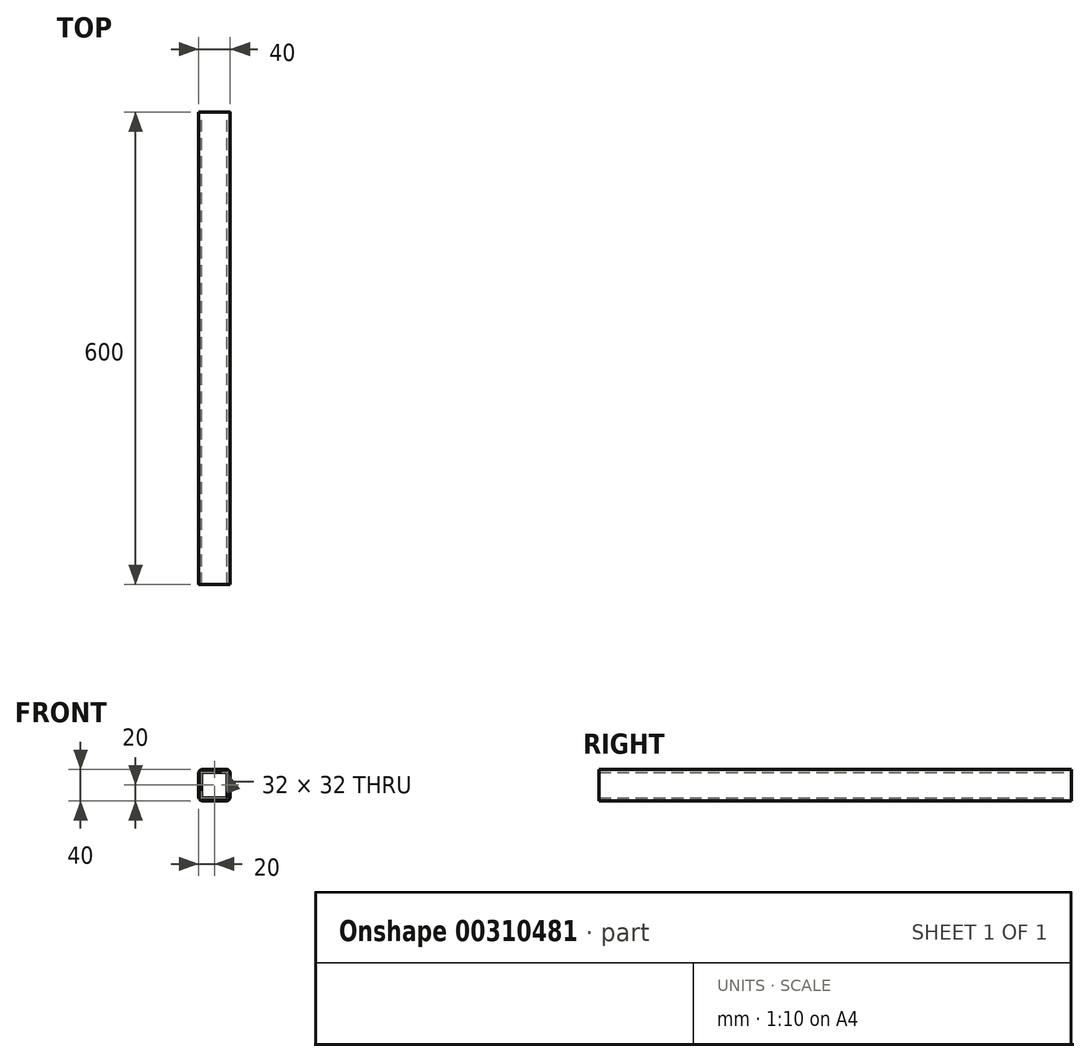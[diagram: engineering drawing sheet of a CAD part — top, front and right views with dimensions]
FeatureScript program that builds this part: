
annotation { "Feature Type Name" : "Feature", "Feature Type Description" : "" }
export const myFeature = defineFeature(function(context is Context, id is Id, definition is map)
    precondition{}
    {
        {
            var Q0;
            Q0=qCreatedBy(makeId("Front.planeOp"),FACE);
            var sketch = newSketch(context, id + "F0", { "sketchPlane" : qUnion([Q0])});
            skLineSegment(sketch, "E0.bottom", {"start": v(15, -20) * mm, "end": v(-15, -20) * mm});
            skLineSegment(sketch, "E0.top", {"start": v(15, 20) * mm, "end": v(-15, 20) * mm});
            skLineSegment(sketch, "E0.left", {"start": v(20, -15) * mm, "end": v(20, 15) * mm});
            skLineSegment(sketch, "E0.right", {"start": v(-20, -15) * mm, "end": v(-20, 15) * mm});
            skPoint(sketch, "E0.middle", {"position": v(0, 0) * mm});
            skPoint(sketch, "E1.visualSharp", {"position": v(-20, 20) * mm});
            skArc(sketch, "E1.filletArc", {"start": v(-15, 20) * mm, "mid": v(-18.54, 18.54) * mm, "end": v(-20, 15) * mm});
            skPoint(sketch, "E2.visualSharp", {"position": v(20, 20) * mm});
            skArc(sketch, "E2.filletArc", {"start": v(20, 15) * mm, "mid": v(18.54, 18.54) * mm, "end": v(15, 20) * mm});
            skPoint(sketch, "E3.visualSharp", {"position": v(20, -20) * mm});
            skArc(sketch, "E3.filletArc", {"start": v(15, -20) * mm, "mid": v(18.54, -18.54) * mm, "end": v(20, -15) * mm});
            skPoint(sketch, "E4.visualSharp", {"position": v(-20, -20) * mm});
            skArc(sketch, "E4.filletArc", {"start": v(-20, -15) * mm, "mid": v(-18.54, -18.54) * mm, "end": v(-15, -20) * mm});
            skLineSegment(sketch, "E5.0", {"start": v(-16, -16) * mm, "end": v(-16, 16) * mm});
            skLineSegment(sketch, "E5.1", {"start": v(16, -16) * mm, "end": v(-16, -16) * mm});
            skLineSegment(sketch, "E5.2", {"start": v(16, -16) * mm, "end": v(16, 16) * mm});
            skLineSegment(sketch, "E5.3", {"start": v(16, 16) * mm, "end": v(-16, 16) * mm});
            skSolve(sketch);
        }
        {
            var Q0;
            Q0=makeQuery(id+"F0.imprint","IMPRINT",FACE,{"disambiguationData":[TD([[makeQuery(id+"F0.imprint","IMPRINT",EDGE,{"derivedFrom":sQuery(id+"F0.wireOp",EDGE,"E0.bottom")}),-1.0]])]});
            extrude(context, id + "F1", {"entities" : qUnion([Q0]), "depth" : 600 * mm});
        }
    });
